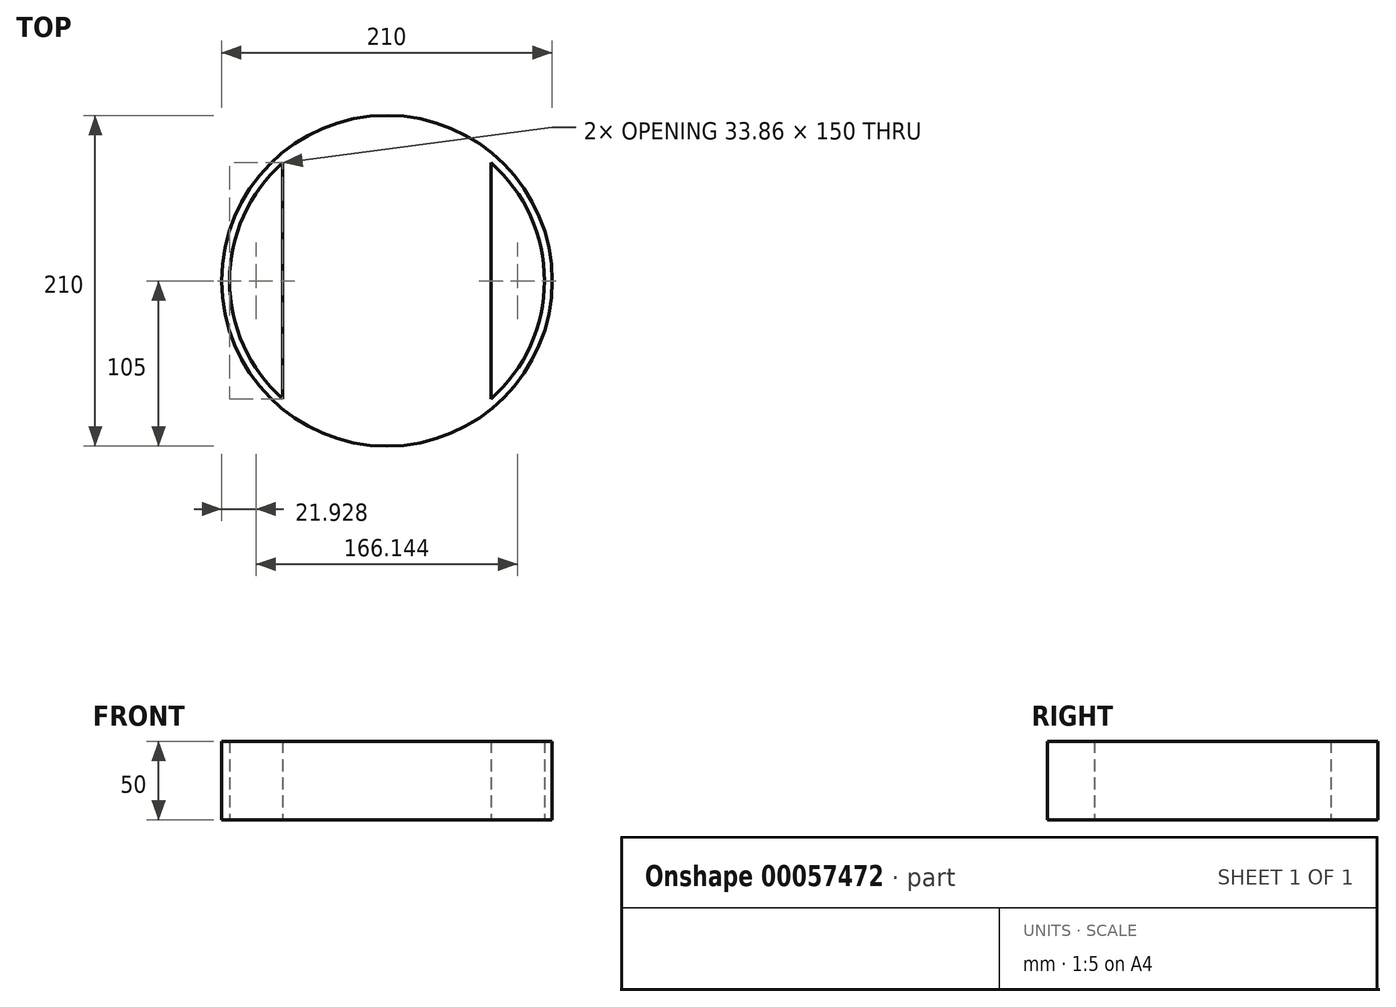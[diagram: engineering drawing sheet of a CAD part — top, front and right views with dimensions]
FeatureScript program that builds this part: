
annotation { "Feature Type Name" : "Feature", "Feature Type Description" : "" }
export const myFeature = defineFeature(function(context is Context, id is Id, definition is map)
    precondition{}
    {
        {
            var Q0;
            Q0=qCreatedBy(makeId("Top.planeOp"),FACE);
            var sketch = newSketch(context, id + "F0", { "sketchPlane" : qUnion([Q0])});
            skCircle(sketch, "E0", {"center": v(0, 0) * mm, "radius": 100 * mm});
            skCircle(sketch, "E1.0", {"center": v(0, 0) * mm, "radius": 105 * mm});
            skSolve(sketch);
        }
        {
            var Q0;
            Q0=makeQuery(id+"F0.imprint","IMPRINT",FACE,{"disambiguationData":[TD([[makeQuery(id+"F0.imprint","IMPRINT",EDGE,{"derivedFrom":sQuery(id+"F0.wireOp",EDGE,"E0")}),-1.0]])]});
            extrude(context, id + "F1", {"entities" : qUnion([Q0]), "depth" : 50 * mm});
        }
        {
            var Q0;
            Q0=qCreatedBy(makeId("Front.planeOp"),FACE);
            cPlane(context, id + "F2", {"entities" : qUnion([Q0]), "cplaneType" : CPlaneType.OFFSET, "offset" : 75 * mm, "width" : 150 * mm, "height" : 150 * mm});
        }
        {
            var Q0;
            Q0=qCreatedBy(id+"F2.planeOp",FACE);
            var sketch = newSketch(context, id + "F3", { "sketchPlane" : qUnion([Q0])});
            skLineSegment(sketch, "E2.bottom", {"start": v(-66.14, 50) * mm, "end": v(66.14, 50) * mm});
            skLineSegment(sketch, "E2.top", {"start": v(-66.14, 0) * mm, "end": v(66.14, 0) * mm});
            skLineSegment(sketch, "E2.left", {"start": v(-66.14, 50) * mm, "end": v(-66.14, 0) * mm});
            skLineSegment(sketch, "E2.right", {"start": v(66.14, 50) * mm, "end": v(66.14, 0) * mm});
            skSolve(sketch);
        }
        {
            var Q0;
            Q0=makeQuery(id+"F3.imprint","IMPRINT",FACE,{"disambiguationData":[TD([[makeQuery(id+"F3.imprint","IMPRINT",EDGE,{"derivedFrom":sQuery(id+"F3.wireOp",EDGE,"E2.bottom")}),-1.0]])]});
            var Q1;
            Q1=makeQuery(id+"F1.opExtrude","SWEPT_FACE",FACE,{"disambiguationData":[OSD([sQuery(id+"F0.wireOp",EDGE,"E0")])]});
            extrude(context, id + "F4", {"entities" : qUnion([Q0]), "operationType" : NewBodyOperationType.ADD, "endBound" : BoundingType.UP_TO_SURFACE, "endBoundEntityFace" : qUnion([Q1]), "depth" : 25 * mm});
        }
        {
            var Q0;
            Q0=makeQuery(id+"F4.opExtrude","CAP_FACE",FACE,{"disambiguationData":[OSD([sQuery(id+"F3.wireOp",EDGE,"E2.bottom"),sQuery(id+"F3.wireOp",EDGE,"E2.top"),sQuery(id+"F3.wireOp",EDGE,"E2.left"),sQuery(id+"F3.wireOp",EDGE,"E2.right")])],"isStart":true});
            var Q1;
            Q1=makeQuery(id+"F1.opExtrude","SWEPT_FACE",FACE,{"disambiguationData":[OSD([sQuery(id+"F0.wireOp",EDGE,"E0")])]});
            extrude(context, id + "F5", {"entities" : qUnion([Q0]), "operationType" : NewBodyOperationType.ADD, "endBound" : BoundingType.UP_TO_SURFACE, "endBoundEntityFace" : qUnion([Q1]), "depth" : 25 * mm});
        }
    });
